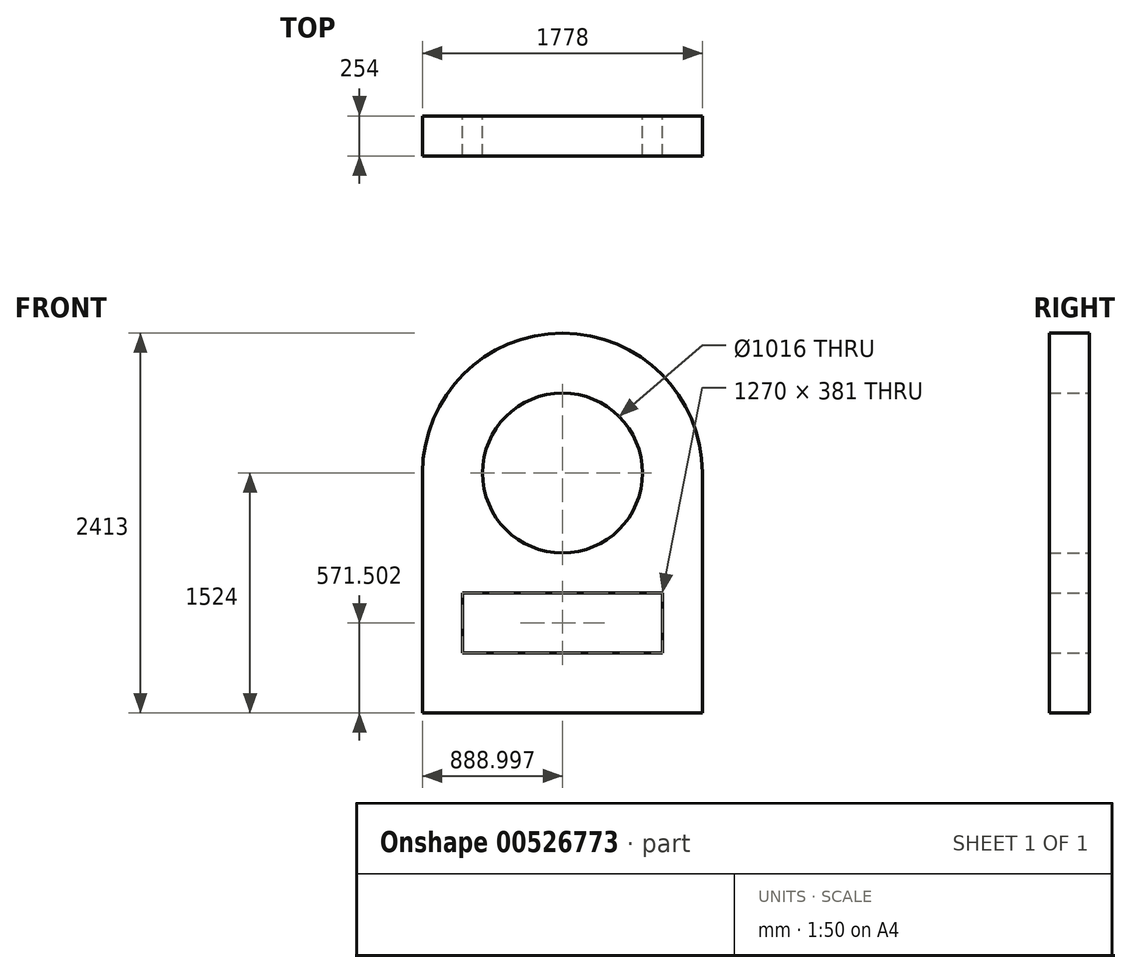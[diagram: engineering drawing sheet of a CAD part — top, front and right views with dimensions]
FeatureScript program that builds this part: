
annotation { "Feature Type Name" : "Feature", "Feature Type Description" : "" }
export const myFeature = defineFeature(function(context is Context, id is Id, definition is map)
    precondition{}
    {
        {
            var Q0;
            Q0=qCreatedBy(makeId("Front.planeOp"),FACE);
            var sketch = newSketch(context, id + "F0", { "sketchPlane" : qUnion([Q0])});
            skLineSegment(sketch, "E0", {"start": v(-9.65, -218.86) * mm, "end": v(1768.35, -218.86) * mm});
            skLineSegment(sketch, "E1", {"start": v(1768.35, -218.86) * mm, "end": v(1768.35, 1305.14) * mm});
            skLineSegment(sketch, "E2", {"start": v(-9.65, -218.86) * mm, "end": v(-9.65, 1305.14) * mm});
            skArc(sketch, "E3", {"start": v(1768.35, 1305.14) * mm, "mid": v(879.35, 2194.14) * mm, "end": v(-9.65, 1305.14) * mm});
            skCircle(sketch, "E4", {"center": v(879.35, 1305.14) * mm, "radius": 508 * mm});
            skLineSegment(sketch, "E5", {"start": v(244.35, 162.14) * mm, "end": v(1514.35, 162.14) * mm});
            skLineSegment(sketch, "E6", {"start": v(1514.35, 162.14) * mm, "end": v(1514.35, 543.14) * mm});
            skLineSegment(sketch, "E7", {"start": v(1514.35, 543.14) * mm, "end": v(244.35, 543.14) * mm});
            skLineSegment(sketch, "E8", {"start": v(244.35, 543.14) * mm, "end": v(244.35, 162.14) * mm});
            skSolve(sketch);
        }
        {
            var Q0;
            Q0=makeQuery(id+"F0.imprint","IMPRINT",FACE,{"disambiguationData":[TD([[makeQuery(id+"F0.imprint","IMPRINT",EDGE,{"derivedFrom":sQuery(id+"F0.wireOp",EDGE,"E0")}),1.0]])]});
            extrude(context, id + "F1", {"entities" : qUnion([Q0]), "depth" : 254 * mm, "offsetDistance" : 25.4 * mm});
        }
    });
